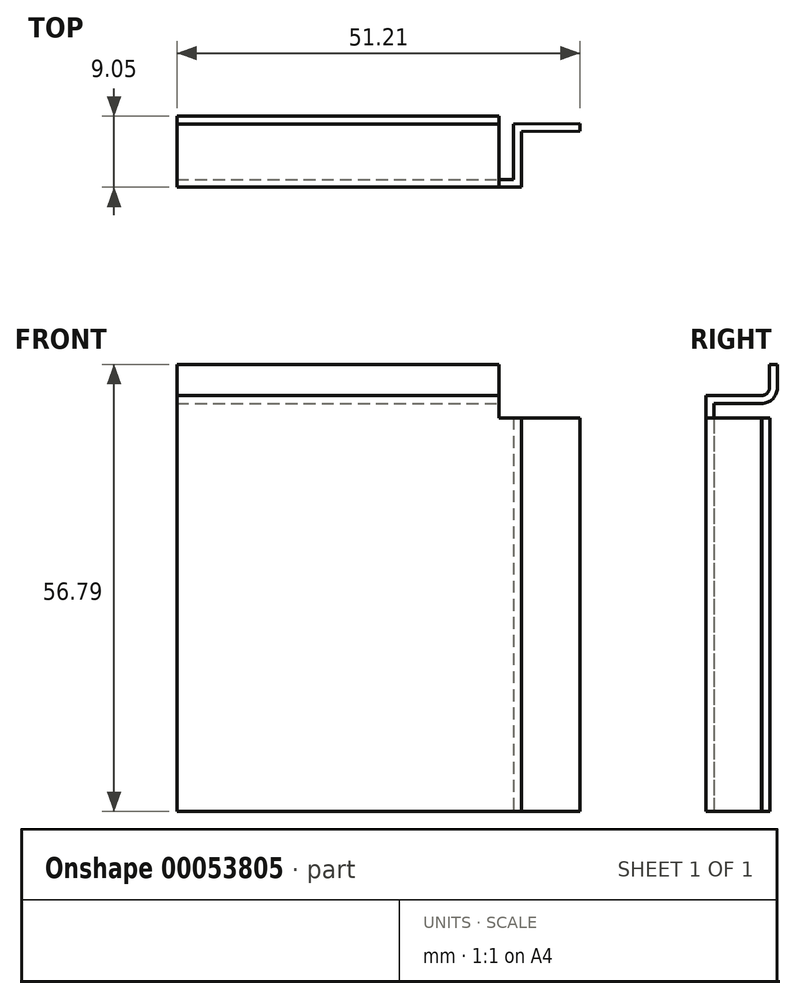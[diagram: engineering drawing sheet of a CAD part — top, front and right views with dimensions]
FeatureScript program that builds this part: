
annotation { "Feature Type Name" : "Feature", "Feature Type Description" : "" }
export const myFeature = defineFeature(function(context is Context, id is Id, definition is map)
    precondition{}
    {
        {
            var Q0;
            Q0=qCreatedBy(makeId("Top.planeOp"),FACE);
            var sketch = newSketch(context, id + "F0", { "sketchPlane" : qUnion([Q0])});
            skLineSegment(sketch, "E0", {"start": v(0, 0) * mm, "end": v(0, 55.46) * mm, "construction": true});
            skLineSegment(sketch, "E1", {"start": v(0, 0) * mm, "end": v(42.77, 0) * mm});
            skLineSegment(sketch, "E2", {"start": v(42.77, 0) * mm, "end": v(42.77, 7.05) * mm});
            skLineSegment(sketch, "E3", {"start": v(42.77, 7.05) * mm, "end": v(51.2, 7.12) * mm});
            skLineSegment(sketch, "E4.0", {"start": v(43.77, 6.06) * mm, "end": v(51.21, 6.12) * mm});
            skLineSegment(sketch, "E4.1", {"start": v(43.77, -1) * mm, "end": v(43.77, 6.06) * mm});
            skLineSegment(sketch, "E4.2", {"start": v(0, -1) * mm, "end": v(43.77, -1) * mm});
            skLineSegment(sketch, "E5", {"start": v(51.2, 7.12) * mm, "end": v(51.21, 6.12) * mm});
            skLineSegment(sketch, "E6", {"start": v(0, 0) * mm, "end": v(0, -1) * mm});
            skSolve(sketch);
        }
        {
            var Q0;
            Q0=makeQuery(id+"F0.imprint","IMPRINT",FACE,{"disambiguationData":[TD([[makeQuery(id+"F0.imprint","IMPRINT",EDGE,{"derivedFrom":sQuery(id+"F0.wireOp",EDGE,"E1")}),-1.0]])]});
            extrude(context, id + "F1", {"entities" : qUnion([Q0]), "endBound" : BoundingType.SYMMETRIC, "depth" : 50 * mm});
        }
        {
            var Q0;
            Q0=makeQuery(id+"F1.opExtrude","SWEPT_FACE",FACE,{"disambiguationData":[OSD([sQuery(id+"F0.wireOp",EDGE,"E1")])]});
            var sketch = newSketch(context, id + "F2", { "sketchPlane" : qUnion([Q0])});
            skLineSegment(sketch, "E7.bottom", {"start": v(0, 25) * mm, "end": v(-40.9, 25) * mm});
            skLineSegment(sketch, "E7.top", {"start": v(0, 27.83) * mm, "end": v(-40.9, 27.83) * mm});
            skLineSegment(sketch, "E7.left", {"start": v(0, 25) * mm, "end": v(0, 27.83) * mm});
            skLineSegment(sketch, "E7.right", {"start": v(-40.9, 25) * mm, "end": v(-40.9, 27.83) * mm});
            skSolve(sketch);
        }
        {
            var Q0;
            Q0=makeQuery(id+"F2.imprint","IMPRINT",FACE,{"disambiguationData":[TD([[makeQuery(id+"F2.imprint","IMPRINT",EDGE,{"derivedFrom":sQuery(id+"F2.wireOp",EDGE,"E7.bottom")}),-1.0]])]});
            var Q1;
            Q1=makeQuery(id+"F1.opExtrude","SWEPT_FACE",FACE,{"disambiguationData":[OSD([sQuery(id+"F0.wireOp",EDGE,"E4.2")])]});
            extrude(context, id + "F3", {"entities" : qUnion([Q0]), "operationType" : NewBodyOperationType.ADD, "endBound" : BoundingType.UP_TO_SURFACE, "oppositeDirection" : true, "endBoundEntityFace" : qUnion([Q1]), "depth" : 25 * mm});
        }
        {
            var Q0;
            Q0=makeQuery(id+"F3.opExtrude","SWEPT_FACE",FACE,{"disambiguationData":[OSD([sQuery(id+"F2.wireOp",EDGE,"E7.right")])]});
            var sketch = newSketch(context, id + "F4", { "sketchPlane" : qUnion([Q0])});
            skLineSegment(sketch, "E8", {"start": v(0, 27.83) * mm, "end": v(7.05, 27.83) * mm});
            skLineSegment(sketch, "E9", {"start": v(7.05, 27.83) * mm, "end": v(7.05, 31.79) * mm});
            skLineSegment(sketch, "E10.0", {"start": v(8.05, 26.83) * mm, "end": v(8.05, 31.79) * mm});
            skLineSegment(sketch, "E10.1", {"start": v(0, 26.83) * mm, "end": v(8.05, 26.83) * mm});
            skLineSegment(sketch, "E11", {"start": v(8.05, 31.79) * mm, "end": v(7.05, 31.79) * mm});
            skLineSegment(sketch, "E12", {"start": v(0, 27.83) * mm, "end": v(0, 26.83) * mm});
            skSolve(sketch);
        }
        {
            var Q0;
            Q0=makeQuery(id+"F4.imprint","IMPRINT",FACE,{"disambiguationData":[TD([[makeQuery(id+"F4.imprint","IMPRINT",EDGE,{"derivedFrom":sQuery(id+"F4.wireOp",EDGE,"E8")}),-1.0]])]});
            var Q1;
            Q1=makeQuery(id+"F3.boolean.opBoolean","MERGE",FACE,{"derivedFrom":[makeQuery(id+"F1.opExtrude","SWEPT_FACE",FACE,{"disambiguationData":[OSD([sQuery(id+"F0.wireOp",EDGE,"E6")])]}),makeQuery(id+"F3.opExtrude","SWEPT_FACE",FACE,{"disambiguationData":[OSD([sQuery(id+"F2.wireOp",EDGE,"E7.left")])]})]});
            extrude(context, id + "F5", {"entities" : qUnion([Q0]), "operationType" : NewBodyOperationType.ADD, "endBound" : BoundingType.UP_TO_SURFACE, "oppositeDirection" : true, "endBoundEntityFace" : qUnion([Q1]), "depth" : 25 * mm});
        }
        {
            var Q0;
            Q0=makeQuery(id+"F5.opExtrude","SWEPT_EDGE",EDGE,{"disambiguationData":[OSD([sQuery(id+"F4.wireOp",EDGE,"E8"),sQuery(id+"F4.wireOp",EDGE,"E9")])]});
            fillet(context, id + "F6", {"entities" : qUnion([Q0]), "radius" : 1 * mm, "tangentPropagation" : true, "allowEdgeOverflow" : false});
        }
        {
            var Q0;
            Q0=makeQuery(id+"F5.opExtrude","SWEPT_EDGE",EDGE,{"disambiguationData":[OSD([sQuery(id+"F4.wireOp",EDGE,"E10.0"),sQuery(id+"F4.wireOp",EDGE,"E10.1")])]});
            fillet(context, id + "F7", {"entities" : qUnion([Q0]), "radius" : 2 * mm, "tangentPropagation" : true, "allowEdgeOverflow" : false});
        }
    });
